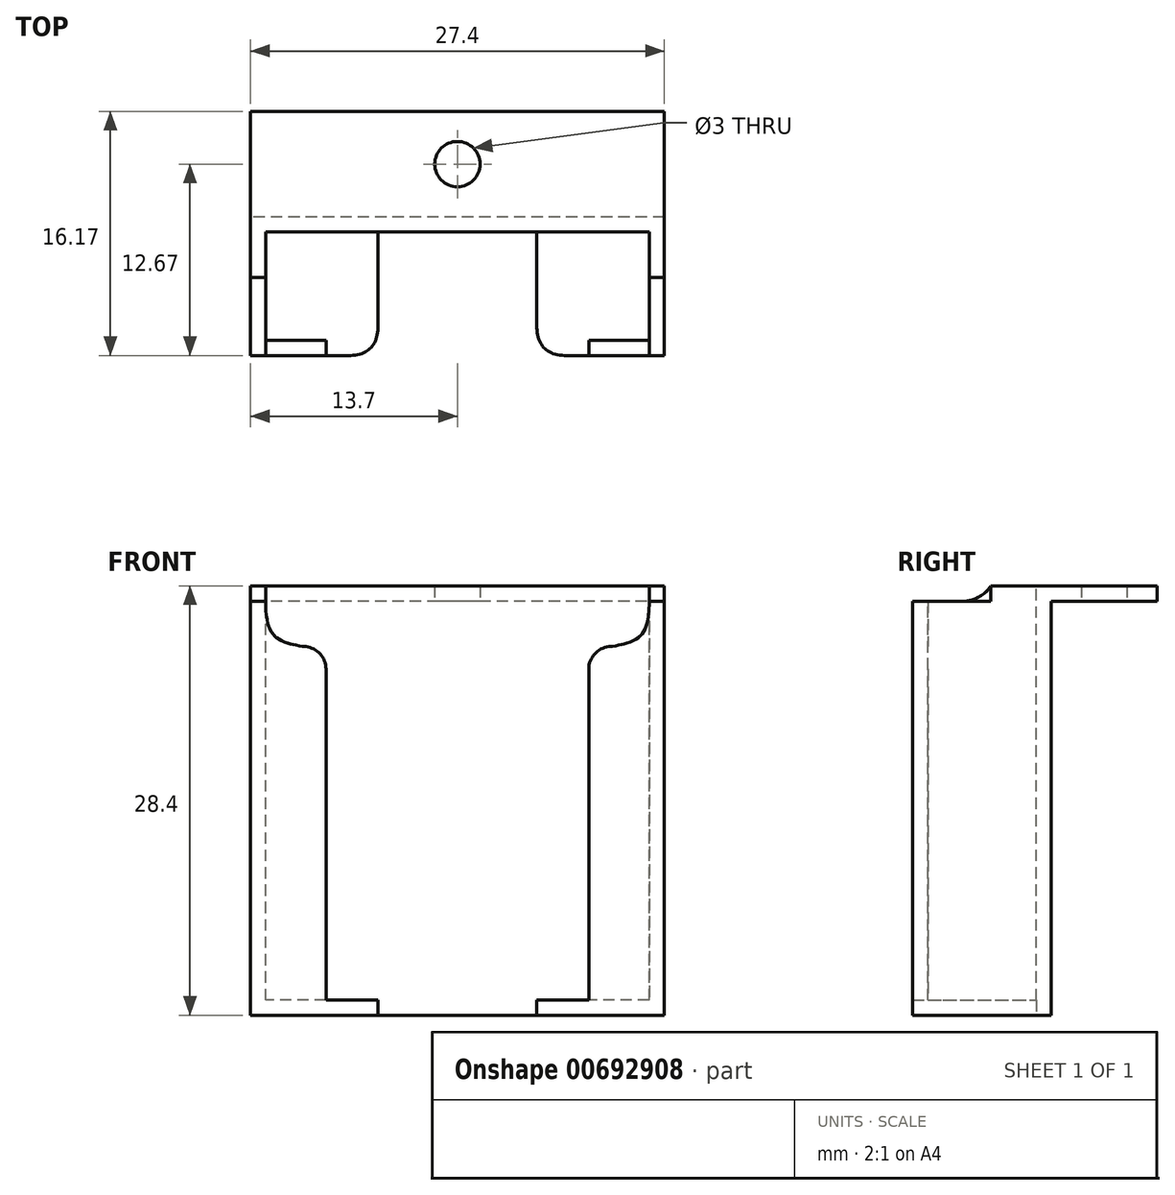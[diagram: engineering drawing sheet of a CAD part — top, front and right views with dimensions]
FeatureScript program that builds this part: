
annotation { "Feature Type Name" : "Feature", "Feature Type Description" : "" }
export const myFeature = defineFeature(function(context is Context, id is Id, definition is map)
    precondition{}
    {
        {
            assignVariable(context, id + "F0", {"name" : "thickness", "anyValue" : 1 * mm});
        }
        {
            var Q0;
            Q0=qCreatedBy(makeId("Front.planeOp"),FACE);
            var sketch = newSketch(context, id + "F1", { "sketchPlane" : qUnion([Q0])});
            skLineSegment(sketch, "E0.bottom", {"start": v(12.7, 12.7) * mm, "end": v(-12.7, 12.7) * mm, "construction": true});
            skLineSegment(sketch, "E0.top", {"start": v(12.7, -12.7) * mm, "end": v(5.25, -12.7) * mm});
            skLineSegment(sketch, "E0.left", {"start": v(12.7, 12.7) * mm, "end": v(12.7, -12.7) * mm});
            skLineSegment(sketch, "E0.right", {"start": v(-12.7, 12.7) * mm, "end": v(-12.7, -12.7) * mm});
            skPoint(sketch, "E0.middle", {"position": v(0, 0) * mm});
            skLineSegment(sketch, "E1.0", {"start": v(-13.7, 13.7) * mm, "end": v(-13.7, -13.7) * mm});
            skLineSegment(sketch, "E1.1", {"start": v(13.7, 13.7) * mm, "end": v(-13.7, 13.7) * mm});
            skLineSegment(sketch, "E1.2", {"start": v(13.7, 13.7) * mm, "end": v(13.7, -13.7) * mm});
            skLineSegment(sketch, "E1.3", {"start": v(13.7, -13.7) * mm, "end": v(-13.7, -13.7) * mm});
            skLineSegment(sketch, "E2", {"start": v(-12.7, 12.7) * mm, "end": v(-12.7, 13.7) * mm});
            skLineSegment(sketch, "E3", {"start": v(12.7, 12.7) * mm, "end": v(12.7, 13.7) * mm});
            skLineSegment(sketch, "E4", {"start": v(-5.25, -12.7) * mm, "end": v(-5.25, -13.7) * mm});
            skLineSegment(sketch, "E5", {"start": v(5.25, -12.7) * mm, "end": v(5.25, -13.7) * mm});
            skLineSegment(sketch, "E6", {"start": v(-5.25, -12.7) * mm, "end": v(-12.7, -12.7) * mm});
            skLineSegment(sketch, "E7", {"start": v(-5.25, -12.7) * mm, "end": v(5.25, -12.7) * mm, "construction": true});
            skPoint(sketch, "E8", {"position": v(0, -12.7) * mm});
            skSolve(sketch);
        }
        {
            var Q0;
            Q0=makeQuery(id+"F1.imprint","IMPRINT",FACE,{"disambiguationData":[TD([[makeQuery(id+"F1.imprint","IMPRINT",EDGE,{"derivedFrom":sQuery(id+"F1.wireOp",EDGE,"E0.top")}),-1.0]])]});
            extrude(context, id + "F2", {"entities" : qUnion([Q0]), "depth" : getVariable(context, 'thickness'), "offsetDistance" : 25 * mm});
        }
        {
            var Q0;
            Q0=makeQuery(id+"F1.imprint","IMPRINT",FACE,{"disambiguationData":[TD([[makeQuery(id+"F1.imprint","IMPRINT",EDGE,{"derivedFrom":sQuery(id+"F1.wireOp",EDGE,"E0.top")}),1.0]])]});
            var Q1;
            Q1=makeQuery(id+"F1.imprint","IMPRINT",FACE,{"disambiguationData":[TD([[makeQuery(id+"F1.imprint","IMPRINT",EDGE,{"derivedFrom":sQuery(id+"F1.wireOp",EDGE,"E0.right")}),-1.0]])]});
            extrude(context, id + "F3", {"entities" : qUnion([Q0, Q1]), "operationType" : NewBodyOperationType.ADD, "depth" : 2 * getVariable(context, 'thickness') + 7.17 * mm, "offsetDistance" : 25 * mm});
        }
        {
            var Q0;
            Q0=makeQuery(id+"F3.opExtrude","CAP_EDGE",EDGE,{"disambiguationData":[OSD([sQuery(id+"F1.wireOp",EDGE,"E4")])],"isStart":false});
            var Q1;
            Q1=makeQuery(id+"F3.opExtrude","CAP_EDGE",EDGE,{"disambiguationData":[OSD([sQuery(id+"F1.wireOp",EDGE,"E5")])],"isStart":false});
            fillet(context, id + "F4", {"entities" : qUnion([Q0, Q1]), "radius" : 2 * mm, "tangentPropagation" : true, "rho" : 0.5, "crossSection" : FilletCrossSection.CONIC, "allowEdgeOverflow" : false});
        }
        {
            var Q0;
            Q0=makeQuery(id+"F3.opExtrude","CAP_FACE",FACE,{"disambiguationData":[OSD([sQuery(id+"F1.wireOp",EDGE,"E0.right"),sQuery(id+"F1.wireOp",EDGE,"E1.0"),sQuery(id+"F1.wireOp",EDGE,"E1.1"),sQuery(id+"F1.wireOp",EDGE,"E1.3"),sQuery(id+"F1.wireOp",EDGE,"E2"),sQuery(id+"F1.wireOp",EDGE,"E4"),sQuery(id+"F1.wireOp",EDGE,"E6")])],"isStart":false});
            var sketch = newSketch(context, id + "F5", { "sketchPlane" : qUnion([Q0])});
            skLineSegment(sketch, "E9.bottom", {"start": v(-13.7, 10.7) * mm, "end": v(-10.2, 10.7) * mm});
            skLineSegment(sketch, "E9.top", {"start": v(-13.7, -13.7) * mm, "end": v(-8.7, -13.7) * mm});
            skLineSegment(sketch, "E9.left", {"start": v(-13.7, 10.7) * mm, "end": v(-13.7, -13.7) * mm});
            skLineSegment(sketch, "E9.right", {"start": v(-8.7, 9.2) * mm, "end": v(-8.7, -13.7) * mm});
            skPoint(sketch, "E10.visualSharp", {"position": v(-8.7, 10.7) * mm});
            skArc(sketch, "E10.filletArc", {"start": v(-8.7, 9.2) * mm, "mid": v(-9.14, 10.26) * mm, "end": v(-10.2, 10.7) * mm});
            skLineSegment(sketch, "E11.MirrorCS", {"start": v(13.7, 10.7) * mm, "end": v(10.2, 10.7) * mm});
            skLineSegment(sketch, "E12.MirrorCS", {"start": v(13.7, 10.7) * mm, "end": v(13.7, -13.7) * mm});
            skPoint(sketch, "E13.MirrorP", {"position": v(8.7, 10.7) * mm});
            skArc(sketch, "E14.MirrorCS", {"start": v(8.7, 9.2) * mm, "mid": v(9.14, 10.26) * mm, "end": v(10.2, 10.7) * mm});
            skLineSegment(sketch, "E15.MirrorCS", {"start": v(8.7, 9.2) * mm, "end": v(8.7, -13.7) * mm});
            skLineSegment(sketch, "E16.MirrorCS", {"start": v(13.7, -13.7) * mm, "end": v(8.7, -13.7) * mm});
            skSolve(sketch);
        }
        {
            var Q0;
            Q0=makeQuery(id+"F5.imprint","IMPRINT",FACE,{"disambiguationData":[TD([[makeQuery(id+"F5.imprint","IMPRINT",EDGE,{"derivedFrom":sQuery(id+"F5.wireOp",EDGE,"E11.MirrorCS")}),1.0]])]});
            var Q1;
            {var subQ1=sQuery(id+"F5.wireOp",EDGE,"E9.top");Q1=makeQuery(id+"F5.imprint","IMPRINT",FACE,{"disambiguationData":[TD([[makeQuery(id+"F5.imprint","IMPRINT",EDGE,{"derivedFrom":subQ1}),-1.0]])]});}
            var Q2;
            {var subQ5=sQuery(id+"F5.wireOp",EDGE,"E10.filletArc");Q2=makeQuery(id+"F5.imprint","IMPRINT",FACE,{"disambiguationData":[TD([[makeQuery(id+"F5.imprint","IMPRINT",EDGE,{"derivedFrom":subQ5}),1.0]])]});}
            extrude(context, id + "F6", {"entities" : qUnion([Q0, Q1, Q2]), "operationType" : NewBodyOperationType.ADD, "oppositeDirection" : true, "depth" : getVariable(context, 'thickness'), "offsetDistance" : 25 * mm});
        }
        {
            var Q0;
            Q0=makeQuery(id+"F6.boolean.opBoolean","INTERSECT",EDGE,{"derivedFrom":[makeQuery(id+"F3.opExtrude","SWEPT_FACE",FACE,{"disambiguationData":[OSD([sQuery(id+"F1.wireOp",EDGE,"E0.right"),sQuery(id+"F1.wireOp",EDGE,"E2")])]}),makeQuery(id+"F6.opExtrude","SWEPT_FACE",FACE,{"disambiguationData":[OSD([sQuery(id+"F5.wireOp",EDGE,"E9.bottom")])]})]});
            var Q1;
            Q1=makeQuery(id+"F6.boolean.opBoolean","INTERSECT",EDGE,{"derivedFrom":[makeQuery(id+"F3.opExtrude","SWEPT_FACE",FACE,{"disambiguationData":[OSD([sQuery(id+"F1.wireOp",EDGE,"E0.left"),sQuery(id+"F1.wireOp",EDGE,"E3")])]}),makeQuery(id+"F6.opExtrude","SWEPT_FACE",FACE,{"disambiguationData":[OSD([sQuery(id+"F5.wireOp",EDGE,"E11.MirrorCS")])]})]});
            fillet(context, id + "F7", {"entities" : qUnion([Q0, Q1]), "radius" : 3 * mm, "tangentPropagation" : true, "rho" : 0.6, "crossSection" : FilletCrossSection.CONIC, "allowEdgeOverflow" : false});
        }
        {
            var Q0;
            {var subQ0=sQuery(id+"F1.wireOp",EDGE,"E1.1");Q0=makeQuery(id+"F3.boolean.opBoolean","MERGE",FACE,{"derivedFrom":[makeQuery(id+"F2.opExtrude","SWEPT_FACE",FACE,{"disambiguationData":[OSD([subQ0])]}),makeQuery(id+"F3.opExtrude","SWEPT_FACE",FACE,{"disambiguationData":[OSD([subQ0]),TDD([makeQuery(id+"F1.imprint","IMPRINT",EDGE,{"disambiguationData":[TD([[makeQuery(id+"F1.imprint","INTERSECT",VERTEX,{"derivedFrom":[subQ0,sQuery(id+"F1.wireOp",EDGE,"E1.2")]}),-1.0]])],"derivedFrom":subQ0})])]}),makeQuery(id+"F3.opExtrude","SWEPT_FACE",FACE,{"disambiguationData":[OSD([subQ0]),TDD([makeQuery(id+"F1.imprint","IMPRINT",EDGE,{"disambiguationData":[TD([[makeQuery(id+"F1.imprint","INTERSECT",VERTEX,{"derivedFrom":[sQuery(id+"F1.wireOp",EDGE,"E1.0"),subQ0]}),1.0]])],"derivedFrom":subQ0})])]})]});}
            var sketch = newSketch(context, id + "F8", { "sketchPlane" : qUnion([Q0])});
            skLineSegment(sketch, "E17.bottom", {"start": v(-13.7, -1) * mm, "end": v(13.7, -1) * mm});
            skLineSegment(sketch, "E17.top", {"start": v(-13.7, 7) * mm, "end": v(13.7, 7) * mm});
            skLineSegment(sketch, "E17.left", {"start": v(-13.7, -1) * mm, "end": v(-13.7, 7) * mm});
            skLineSegment(sketch, "E17.right", {"start": v(13.7, -1) * mm, "end": v(13.7, 7) * mm});
            skLineSegment(sketch, "E18", {"start": v(-13.7, 0) * mm, "end": v(13.7, 0) * mm, "construction": true});
            skLineSegment(sketch, "E19", {"start": v(0, 7) * mm, "end": v(0, 0) * mm, "construction": true});
            skPoint(sketch, "E20", {"position": v(0, 3.5) * mm});
            skCircle(sketch, "E21", {"center": v(0, 3.5) * mm, "radius": 1.5 * mm});
            skLineSegment(sketch, "E22", {"start": v(13.7, -4) * mm, "end": v(12.7, -4) * mm});
            skLineSegment(sketch, "E23", {"start": v(12.7, -4) * mm, "end": v(12.7, 0) * mm});
            skLineSegment(sketch, "E24", {"start": v(13.7, -4) * mm, "end": v(13.7, -1) * mm});
            skLineSegment(sketch, "E25.MirrorCS", {"start": v(-12.7, -4) * mm, "end": v(-12.7, 0) * mm});
            skLineSegment(sketch, "E26.MirrorCS", {"start": v(-13.7, -4) * mm, "end": v(-12.7, -4) * mm});
            skLineSegment(sketch, "E27.MirrorCS", {"start": v(-13.7, -4) * mm, "end": v(-13.7, -1) * mm});
            skSolve(sketch);
        }
        {
            var Q0;
            {var subQ3=sQuery(id+"F8.wireOp",EDGE,"E17.top");Q0=makeQuery(id+"F8.imprint","IMPRINT",FACE,{"disambiguationData":[TD([[makeQuery(id+"F8.imprint","IMPRINT",EDGE,{"derivedFrom":subQ3}),-1.0]])]});}
            var Q1;
            {var subQ2=sQuery(id+"F1.wireOp",EDGE,"E1.1");var subQ5=sQuery(id+"F1.wireOp",EDGE,"E1.2");var subQ7=sQuery(id+"F1.wireOp",EDGE,"E1.0");var subQ9=makeQuery(id+"F3.boolean.opBoolean","MERGE",EDGE,{"derivedFrom":[makeQuery(id+"F2.opExtrude","CAP_EDGE",EDGE,{"disambiguationData":[OSD([subQ2])],"isStart":true}),makeQuery(id+"F3.opExtrude","CAP_EDGE",EDGE,{"disambiguationData":[OSD([subQ2]),TDD([makeQuery(id+"F1.imprint","IMPRINT",EDGE,{"disambiguationData":[TD([[makeQuery(id+"F1.imprint","INTERSECT",VERTEX,{"derivedFrom":[subQ2,subQ5]}),-1.0]])],"derivedFrom":subQ2})])],"isStart":true}),makeQuery(id+"F3.opExtrude","CAP_EDGE",EDGE,{"disambiguationData":[OSD([subQ2]),TDD([makeQuery(id+"F1.imprint","IMPRINT",EDGE,{"disambiguationData":[TD([[makeQuery(id+"F1.imprint","INTERSECT",VERTEX,{"derivedFrom":[subQ7,subQ2]}),1.0]])],"derivedFrom":subQ2})])],"isStart":true})]});Q1=makeQuery(id+"F8.imprint","IMPRINT",FACE,{"disambiguationData":[TD([[makeQuery(id+"F8.imprint","IMPRINT",EDGE,{"derivedFrom":subQ9}),1.0]])]});}
            var Q2;
            {var subQ4=sQuery(id+"F8.wireOp",EDGE,"E22");Q2=makeQuery(id+"F8.imprint","IMPRINT",FACE,{"disambiguationData":[TD([[makeQuery(id+"F8.imprint","IMPRINT",EDGE,{"derivedFrom":subQ4}),-1.0]])]});}
            var Q3;
            {var subQ4=sQuery(id+"F8.wireOp",EDGE,"E26.MirrorCS");Q3=makeQuery(id+"F8.imprint","IMPRINT",FACE,{"disambiguationData":[TD([[makeQuery(id+"F8.imprint","IMPRINT",EDGE,{"derivedFrom":subQ4}),1.0]])]});}
            extrude(context, id + "F9", {"entities" : qUnion([Q0, Q1, Q2, Q3]), "operationType" : NewBodyOperationType.ADD, "depth" : getVariable(context, 'thickness'), "offsetDistance" : 25 * mm});
        }
        {
            var Q0;
            Q0=makeQuery(id+"F9.opExtrude","CAP_EDGE",EDGE,{"disambiguationData":[OSD([sQuery(id+"F8.wireOp",EDGE,"E26.MirrorCS")])],"isStart":true});
            var Q1;
            Q1=makeQuery(id+"F9.opExtrude","CAP_EDGE",EDGE,{"disambiguationData":[OSD([sQuery(id+"F8.wireOp",EDGE,"E22")])],"isStart":true});
            fillet(context, id + "F10", {"entities" : qUnion([Q0, Q1]), "radius" : 2 * mm, "tangentPropagation" : true, "rho" : 0.4, "crossSection" : FilletCrossSection.CONIC, "allowEdgeOverflow" : false});
        }
    });
